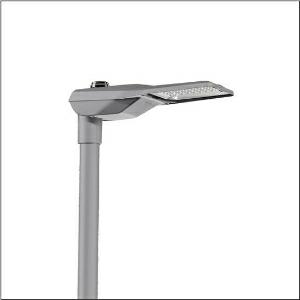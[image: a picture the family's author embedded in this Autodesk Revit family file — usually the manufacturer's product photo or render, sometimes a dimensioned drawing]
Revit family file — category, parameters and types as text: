
# Revit family: streetlight_sl_21_mini___p0_8a_5xe6u47n08hb_863c
name_source: partatom
category: Lighting Fixtures
units: mm (PartAtom-declared; Revit-internal decimal feet)

## family parameters
Cut with Voids When Loaded = No
Host = Face
Light Source = No
Part Type = Normal
Room Calculation Point = No
Round Connector Dimension = Use Diameter
Shared = No

## types (1)
- --- (1 x LED, 9510 lm, 66 W, 4000K)
    Apparent Load = 66 VA
    CIE Flux Codes = 33 69 96 100 100
    Color Rendering = 70
    Color Temperature = 4000K
    Default Elevation = 1800 mm
    Description = Streetlight SL 21 mini, mast luminaire, primary light control with lens, of PMMA, primary optical cover: cover, of toughened safety glass, transparent, light distribution: P0.8a, light emission: direct distribution, primary light characteristic: asymmetric, installation type: side-entry, LED, 3G 1.5mm², High Power LED, rated luminous flux: 9.510lm, luminous efficacy: 144lm/W, light colour: 740, colour temperature: 4000K, control gear: NEMA (7pin), control: flexible luminous flux parameterisation, time-dependent luminous flux control, constant luminous flux control, pre-setting: linear dimming characteristic, overheat protection, mains connection: 230..240V, AC, 50/60Hz, connection cable pre-assembled, cable length: 8,5m, wiring characteristics: H07RN-F, start of lifetime: 66W, end of service life: 69W, reduction: 30W, luminaire housing, of diecast aluminium (EN AC-44300), powder-coated, SITECO metallic grey (DB 702S), corrosivity category C5 high according to DIN EN ISO 12944, multi-level sealing system, sealing non-destructively replaceable, inclination adjustable: 0°, 5°, 10°, 15°, length: 628mm, width: 235mm, height: 110mm, spigot size: 42mm (side-entry), mounting height: 4..8m, protection rating (complete): IP66, insulation class (complete): insulation class I (protective earthing), certification: CE, ENEC, ENEC+, VDE, impact resistance: IK10, permissible operating ambient temperature for outdoor applications: -40..+50°C, standard-compliant lighting for roads and squares, packaging unit: 1 piece

Light Distribution: P0.8a
    Height = 110 mm
    Lamp = 1 x LED
    Lamp Light Flux = 9510 lm
    Lamp Power = 66 W
    Lamp count = 1
    Length = 625 mm
    Luminous efficacy = 144 lm/W
    Manufacturer = Siteco
    ModVariant = No
    Model = 5XE6U47N08HB
    Number of Poles = 1
    OnlyDefault = Yes
    Power Factor = 1
    Product Name = Streetlight SL 21 mini | P0.8a
    Product group = mast luminaire | pylon top
    ProductGroupID = 6100
    Protection Class = Protection class I
    Protection Degree = IP 66
    RLX_Detail_Level = 1
    RLX_Emergency_Light_Flux = 0 lm
    RLX_Emergency_Type = 0
    RLX_Emergency_Type_DB = No
    RlxData = <blob elided: 91853 chars, md5=01381f02>
    Socket = socket
    Standby Power = 0 W
    System Light Flux = 9510 lm
    System Power = 66 W
    Type Comments = factory setting: luminous flux: 100 % | dim-lin: 254 | 670 mA
    Type Image = l_1294379.jpg
    URL = http://relux.com
    VarID = @adj_081245
    Voltage = 0 V
    Weight = 0.00 kg
    Width = 234 mm

## geometry (parser evidence)
native form markers: Blend x4, Sweep x11
no freeform markers — native parametric forms only
